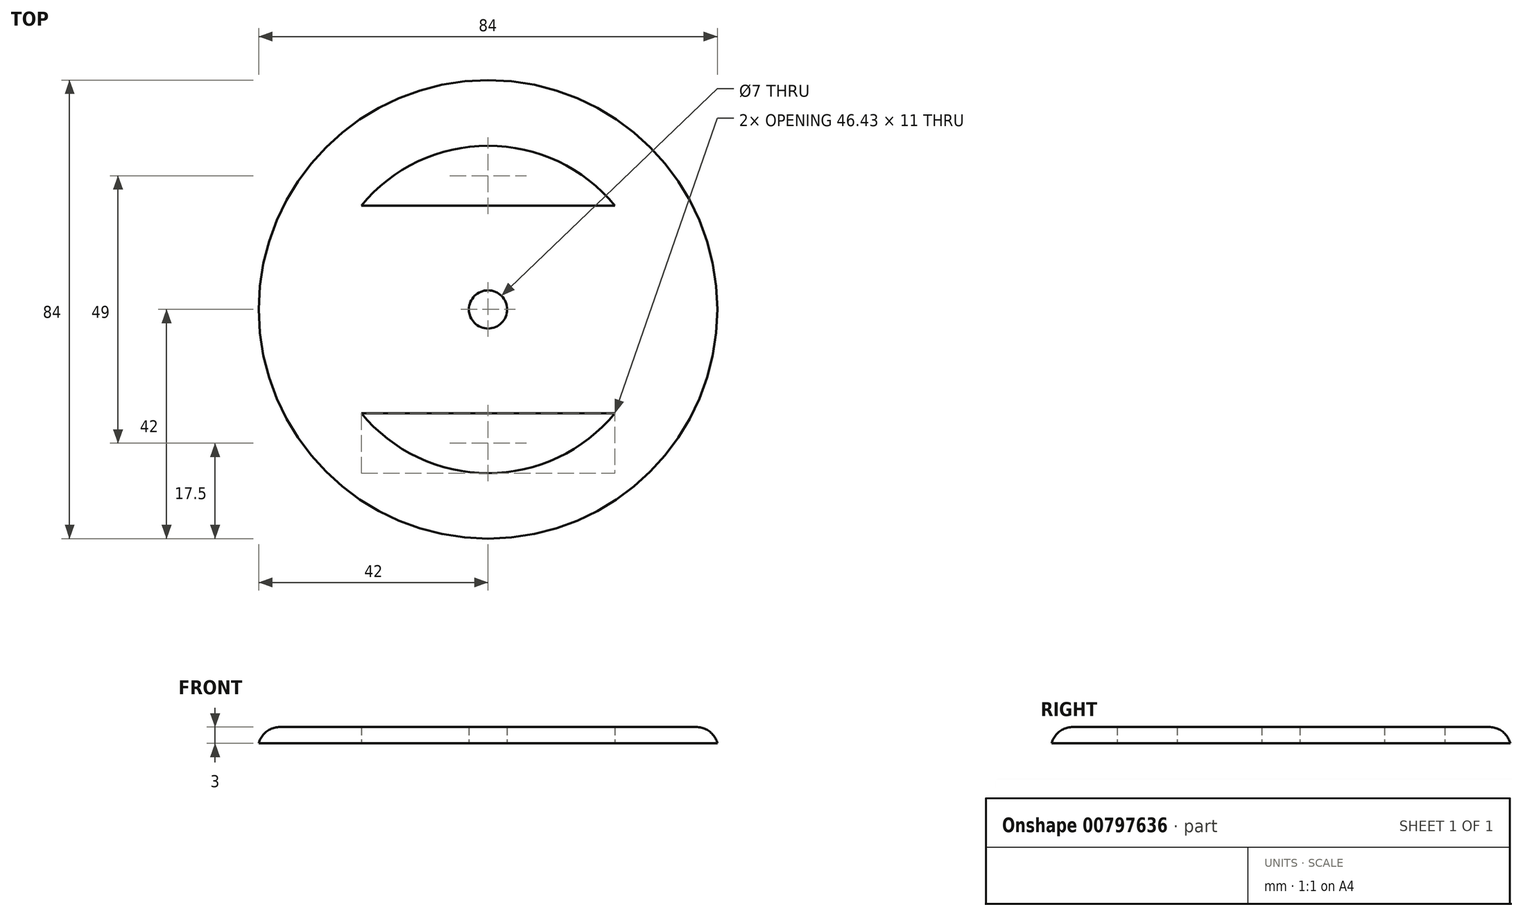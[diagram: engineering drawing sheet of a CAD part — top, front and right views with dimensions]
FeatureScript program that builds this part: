
annotation { "Feature Type Name" : "Feature", "Feature Type Description" : "" }
export const myFeature = defineFeature(function(context is Context, id is Id, definition is map)
    precondition{}
    {
        {
            var Q0;
            Q0=qCreatedBy(makeId("Top.planeOp"),FACE);
            var sketch = newSketch(context, id + "F0", { "sketchPlane" : qUnion([Q0])});
            skLineSegment(sketch, "E0.bottom", {"start": v(27.5, -9) * mm, "end": v(-27.5, -9) * mm});
            skLineSegment(sketch, "E0.top", {"start": v(27.5, 9) * mm, "end": v(-27.5, 9) * mm});
            skLineSegment(sketch, "E0.left", {"start": v(27.5, -9) * mm, "end": v(27.5, 9) * mm});
            skLineSegment(sketch, "E0.right", {"start": v(-27.5, -9) * mm, "end": v(-27.5, 9) * mm});
            skPoint(sketch, "E0.middle", {"position": v(0, 0) * mm});
            skLineSegment(sketch, "E1.bottom", {"start": v(20.5, -10) * mm, "end": v(-20.5, -10) * mm});
            skLineSegment(sketch, "E1.top", {"start": v(20.5, 10) * mm, "end": v(-20.5, 10) * mm});
            skLineSegment(sketch, "E1.left", {"start": v(20.5, -10) * mm, "end": v(20.5, 10) * mm});
            skLineSegment(sketch, "E1.right", {"start": v(-20.5, -10) * mm, "end": v(-20.5, 10) * mm});
            skCircle(sketch, "E2", {"center": v(-24.5, 5) * mm, "radius": 2.25 * mm});
            skLineSegment(sketch, "E3", {"start": v(-27.5, 0) * mm, "end": v(27.5, 0) * mm});
            skCircle(sketch, "E4.MirrorC", {"center": v(-24.5, -5) * mm, "radius": 2.25 * mm});
            skLineSegment(sketch, "E5", {"start": v(0, 9) * mm, "end": v(0, -10) * mm});
            skCircle(sketch, "E6.MirrorC", {"center": v(24.5, -5) * mm, "radius": 2.25 * mm});
            skCircle(sketch, "E7.MirrorC", {"center": v(24.5, 5) * mm, "radius": 2.25 * mm});
            skCircle(sketch, "E8", {"center": v(9.5, 0) * mm, "radius": 3.5 * mm});
            skSolve(sketch);
        }
        {
            var Q0;
            Q0=qCreatedBy(makeId("Top.planeOp"),FACE);
            var sketch = newSketch(context, id + "F1", { "sketchPlane" : qUnion([Q0])});
            skCircle(sketch, "E9", {"center": v(9.5, 0) * mm, "radius": 42 * mm});
            skSolve(sketch);
        }
        {
            var Q0;
            Q0=makeQuery(id+"F1.imprint","IMPRINT",FACE,{"disambiguationData":[TD([[makeQuery(id+"F1.imprint","IMPRINT",EDGE,{"derivedFrom":sQuery(id+"F1.wireOp",EDGE,"E9")}),1.0]])]});
            extrude(context, id + "F2", {"entities" : qUnion([Q0]), "depth" : 3 * mm, "offsetDistance" : 25 * mm});
        }
        {
            var Q0;
            {var subQ0=sQuery(id+"F0.wireOp",EDGE,"E8");var subQ1=sQuery(id+"F0.wireOp",EDGE,"E3");var subQ2=makeQuery(id+"F0.imprint","INTERSECT",VERTEX,{"disambiguationData":[OD(0.0)],"derivedFrom":[subQ1,subQ0]});Q0=makeQuery(id+"F0.imprint","IMPRINT",FACE,{"disambiguationData":[TD([[makeQuery(id+"F0.imprint","IMPRINT",EDGE,{"disambiguationData":[TD([[subQ2,-1.0]])],"derivedFrom":subQ1}),1.0]])]});}
            var Q1;
            {var subQ0=sQuery(id+"F0.wireOp",EDGE,"E8");var subQ1=sQuery(id+"F0.wireOp",EDGE,"E3");var subQ2=makeQuery(id+"F0.imprint","INTERSECT",VERTEX,{"disambiguationData":[OD(0.0)],"derivedFrom":[subQ1,subQ0]});Q1=makeQuery(id+"F0.imprint","IMPRINT",FACE,{"disambiguationData":[TD([[makeQuery(id+"F0.imprint","IMPRINT",EDGE,{"disambiguationData":[TD([[subQ2,-1.0]])],"derivedFrom":subQ1}),-1.0]])]});}
            extrude(context, id + "F3", {"entities" : qUnion([Q0, Q1]), "operationType" : NewBodyOperationType.REMOVE, "oppositeDirection" : true, "depth" : -3 * mm, "offsetDistance" : 25 * mm});
        }
        {
            var Q0;
            Q0=makeQuery(id+"F2.opExtrude","CAP_EDGE",EDGE,{"disambiguationData":[OSD([sQuery(id+"F1.wireOp",EDGE,"E9")])],"isStart":false});
            var Q1;
            {var subQ0=sQuery(id+"F0.wireOp",EDGE,"E1.left");Q1=makeQuery(id+"Fd4zUNGmm9VfFbr_1.opChamfer","BLEND_EDGE",EDGE,{"blendedFrom":[makeQuery(id+"F3.boolean.opBoolean","COPY",EDGE,{"derivedFrom":makeQuery(id+"F3.opExtrude","CAP_EDGE",EDGE,{"disambiguationData":[OSD([subQ0])],"isStart":false})}),makeQuery(id+"F3.boolean.opBoolean","COPY",FACE,{"derivedFrom":makeQuery(id+"F3.opExtrude","SWEPT_FACE",FACE,{"disambiguationData":[OSD([subQ0])]})})],"blendedInto":[makeQuery(id+"F3.boolean.opBoolean","COPY",FACE,{"derivedFrom":makeQuery(id+"F3.opExtrude","SWEPT_FACE",FACE,{"disambiguationData":[OSD([subQ0])]})})]});}
            var Q2;
            {var subQ0=sQuery(id+"F0.wireOp",EDGE,"E1.right");Q2=makeQuery(id+"Fd4zUNGmm9VfFbr_1.opChamfer","BLEND_EDGE",EDGE,{"blendedFrom":[makeQuery(id+"F3.boolean.opBoolean","COPY",EDGE,{"derivedFrom":makeQuery(id+"F3.opExtrude","CAP_EDGE",EDGE,{"disambiguationData":[OSD([subQ0])],"isStart":false})}),makeQuery(id+"F3.boolean.opBoolean","COPY",FACE,{"derivedFrom":makeQuery(id+"F3.opExtrude","SWEPT_FACE",FACE,{"disambiguationData":[OSD([subQ0])]})})],"blendedInto":[makeQuery(id+"F3.boolean.opBoolean","COPY",FACE,{"derivedFrom":makeQuery(id+"F3.opExtrude","SWEPT_FACE",FACE,{"disambiguationData":[OSD([subQ0])]})})]});}
            var Q3;
            {var subQ0=sQuery(id+"F0.wireOp",EDGE,"E0.top");Q3=makeQuery(id+"Fd4zUNGmm9VfFbr_1.opChamfer","BLEND_EDGE",EDGE,{"blendedFrom":[makeQuery(id+"F3.boolean.opBoolean","COPY",EDGE,{"derivedFrom":makeQuery(id+"F3.opExtrude","CAP_EDGE",EDGE,{"disambiguationData":[OSD([subQ0])],"isStart":false})}),makeQuery(id+"F3.boolean.opBoolean","COPY",FACE,{"derivedFrom":makeQuery(id+"F3.opExtrude","SWEPT_FACE",FACE,{"disambiguationData":[OSD([subQ0])]})})],"blendedInto":[makeQuery(id+"F3.boolean.opBoolean","COPY",FACE,{"derivedFrom":makeQuery(id+"F3.opExtrude","SWEPT_FACE",FACE,{"disambiguationData":[OSD([subQ0])]})})]});}
            var Q4;
            {var subQ0=sQuery(id+"F0.wireOp",EDGE,"E0.bottom");Q4=makeQuery(id+"Fd4zUNGmm9VfFbr_1.opChamfer","BLEND_EDGE",EDGE,{"blendedFrom":[makeQuery(id+"F3.boolean.opBoolean","COPY",EDGE,{"derivedFrom":makeQuery(id+"F3.opExtrude","CAP_EDGE",EDGE,{"disambiguationData":[OSD([subQ0])],"isStart":false})}),makeQuery(id+"F3.boolean.opBoolean","COPY",FACE,{"derivedFrom":makeQuery(id+"F3.opExtrude","SWEPT_FACE",FACE,{"disambiguationData":[OSD([subQ0])]})})],"blendedInto":[makeQuery(id+"F3.boolean.opBoolean","COPY",FACE,{"derivedFrom":makeQuery(id+"F3.opExtrude","SWEPT_FACE",FACE,{"disambiguationData":[OSD([subQ0])]})})]});}
            fillet(context, id + "F4", {"entities" : qUnion([Q0, Q1, Q2, Q3, Q4]), "radius" : 4 * mm, "tangentPropagation" : true, "allowEdgeOverflow" : false});
        }
        {
            var Q0;
            Q0=makeQuery(id+"F1.imprint","IMPRINT",FACE,{"disambiguationData":[TD([[makeQuery(id+"F1.imprint","IMPRINT",EDGE,{"derivedFrom":sQuery(id+"F1.wireOp",EDGE,"E9")}),1.0]])]});
            var sketch = newSketch(context, id + "F5", { "sketchPlane" : qUnion([Q0])});
            skArc(sketch, "E10", {"start": v(32.72, 19) * mm, "mid": v(9.5, 30) * mm, "end": v(-13.72, 19) * mm});
            skLineSegment(sketch, "E11", {"start": v(32.72, 19) * mm, "end": v(-13.72, 19) * mm});
            skArc(sketch, "E12.trimOffspring", {"start": v(-13.72, -19) * mm, "mid": v(9.5, -30) * mm, "end": v(32.72, -19) * mm});
            skLineSegment(sketch, "E13", {"start": v(32.72, -19) * mm, "end": v(-13.72, -19) * mm});
            skSolve(sketch);
        }
        {
            var Q0;
            Q0=qSketchRegion(id+"F5",true);
            extrude(context, id + "F6", {"entities" : qUnion([Q0]), "operationType" : NewBodyOperationType.REMOVE, "oppositeDirection" : true, "depth" : -30 * mm, "offsetDistance" : 25 * mm});
        }
    });
